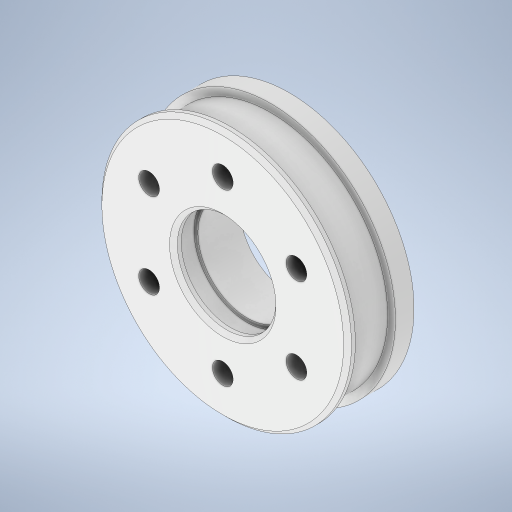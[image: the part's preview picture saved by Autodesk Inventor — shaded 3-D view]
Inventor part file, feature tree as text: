
AUTODESK INVENTOR PART (.ipt)
format: ipt  version: 2024 (Build 280153000, 153)  size: 325,120 bytes
history: native  units: mm
features: extrude x4, sketch x4, projected_geometry x4, plane x3, hole x1, pattern_circular x1, chamfer x1, split x1
ambient origin geometry x8: Origin, YZ Plane, XZ Plane, XY Plane, X Axis, Y Axis, Z Axis, Center Point
bodies: Solid1 (feature_tree), Solid4 (feature_tree), Solid5 (feature_tree)
feature tree (19):
  extrude  "Extrusion1"  Depth=27.2mm
  plane  "Work Plane1"
  plane  "Work Plane2"
  sketch  "Sketch2"  dims[d2=15.0mm d3=0.0mm d4=1.0mm]
  extrude  "Extrusion2"  Depth=15.0mm
  extrude  "Extrusion3"  Depth=15.0mm TaperAngle=0.0deg
  extrude  "Extrusion8"  [1 undecoded]
  hole  "Hole3"  [1 undecoded]
  pattern_circular  "Circular Pattern2"  [2 undecoded]
  chamfer  "Chamfer1"  Distance=60.0mm Angle=360.0deg
  plane  "Work Plane5"
  split  "Split2"
  sketch  "Sketch1"  dims[d0=59.8mm d1=27.2mm]
  projected_geometry  "Projected Loop1"
  sketch  "Sketch8"  dims[d5=-4.25mm d6=15.0mm d7=0.0mm]
  projected_geometry  "Projected Loop8"
  sketch  "Sketch9"  dims[d8=2.0mm d9=-10.25mm d10=10.0mm d11=0.0mm d41=2.0mm d42=0.0mm d43=5.3mm d44=6.0mm d45=4.0mm d46=2.0mm d47=90.0deg d48=8.0mm d49=20.594885mm d50=60.0mm d51=360.0deg d53=1.0mm d54=2.0mm d55=45.0deg]
  projected_geometry  "Projected Loop9"
  projected_geometry  "Projected Loop10"
note: 4 required parameter values undecoded (feature->parameter linkage not recoverable at this tier; creation-order binding heuristic only, values carry confidence <= 0.55)
